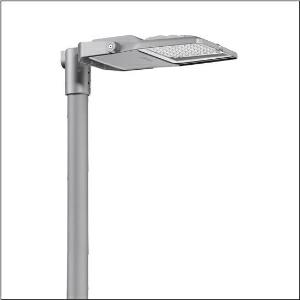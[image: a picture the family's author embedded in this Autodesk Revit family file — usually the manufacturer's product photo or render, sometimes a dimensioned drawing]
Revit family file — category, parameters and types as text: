
# Revit family: floodlight_fl_21_iq_mini___pl33t_5xa7771d2f3a_c3c2
name_source: partatom
category: Lighting Fixtures
units: mm (PartAtom-declared; Revit-internal decimal feet)

## family parameters
Cut with Voids When Loaded = No
Host = Face
Light Source = No
Part Type = Normal
Room Calculation Point = No
Round Connector Dimension = Use Diameter
Shared = No

## types (1)
- --- (1 x LED, 17620 lm, 143 W, 3000K)
    Apparent Load = 143 VA
    CIE Flux Codes = 26 75 99 100 100
    Color Rendering = 70
    Color Temperature = 3000K
    Default Elevation = 1800 mm
    Description = Floodlight FL 21 iQ mini, floodlight, primary light control with lens, of PMMA, primary optical cover: protective disc, of toughened safety glass, transparent, light distribution: PL33T, light emission: direct distribution, installation type: surface-mounted, LED, High Power LED, rated luminous flux: 17.620lm, luminous efficacy: 123lm/W, light colour: 730, colour temperature: 3000K, control: Auto-Match, Temp-Guard, Lumen-Switch, Night-Set, Smart-Wire, Light-Fading, Desk-Remote (wireless, voltage-free reading and setting of iQ features in the workshop via application-optimized NFC function/RFID function), optimised constant luminous flux control (CLO 2.0), with terminal, 6-pole, mains connection: 220..240V, AC, 50/60Hz, start of lifetime: 143W, end of service life: 152W, reduction: 61W, luminaire housing, of diecast aluminium, powder-coated, Siteco® metallic grey (DB 702S), corrosivity category C5 mid according to DIN EN ISO 12944, sealing non-destructively replaceable, please order mast flange separately, mast bracket, of steel, galvanised, powder-coated, Siteco® metallic grey (DB 702S), protection rating (complete): IP66, insulation class (complete): insulation class II (safety insulation), certification: CE, ENEC, VDE, protection symbol: D, impact resistance: IK08, permissible operating ambient temperature: -40..+40°C, permissible operating ambient temperature for outdoor applications: -40..+50°C, standard: DIN EN 12944, LABS conformity tested according to VDMA 24364:2018-05, packaging unit: 1 piece

Light Distribution: PL33T
    Height = 70 mm
    Lamp = 1 x LED
    Lamp Light Flux = 17620 lm
    Lamp Power = 143 W
    Lamp count = 1
    Length = 485 mm
    Luminous efficacy = 123 lm/W
    Manufacturer = Siteco
    ModVariant = No
    Model = 5XA7771D2F3A
    Number of Poles = 1
    OnlyDefault = Yes
    Power Factor = 1
    Product Name = Floodlight FL 21 iQ mini | PL33T
    Product group = floodlight | pylon annexe
    ProductGroupID = 6200
    Protection Class = Protection class II
    Protection Degree = IP 66
    RLX_Detail_Level = 1
    RLX_Emergency_Light_Flux = 0 lm
    RLX_Emergency_Type = 0
    RLX_Emergency_Type_DB = No
    RlxData = <blob elided: 101545 chars, md5=416095d9>
    Socket = socket
    Standby Power = 0 W
    System Light Flux = 17620 lm
    System Power = 143 W
    Type Comments = factory setting: luminous flux: 100 % | dim-lin: 254 | 730 mA
    Type Image = l_1007125.jpg
    URL = http://relux.com
    VarID = @adj_119531
    Voltage = 0 V
    Weight = 0.00 kg
    Width = 337 mm

## geometry (parser evidence)
native form markers: Blend x4, Sweep x11
no freeform markers — native parametric forms only
